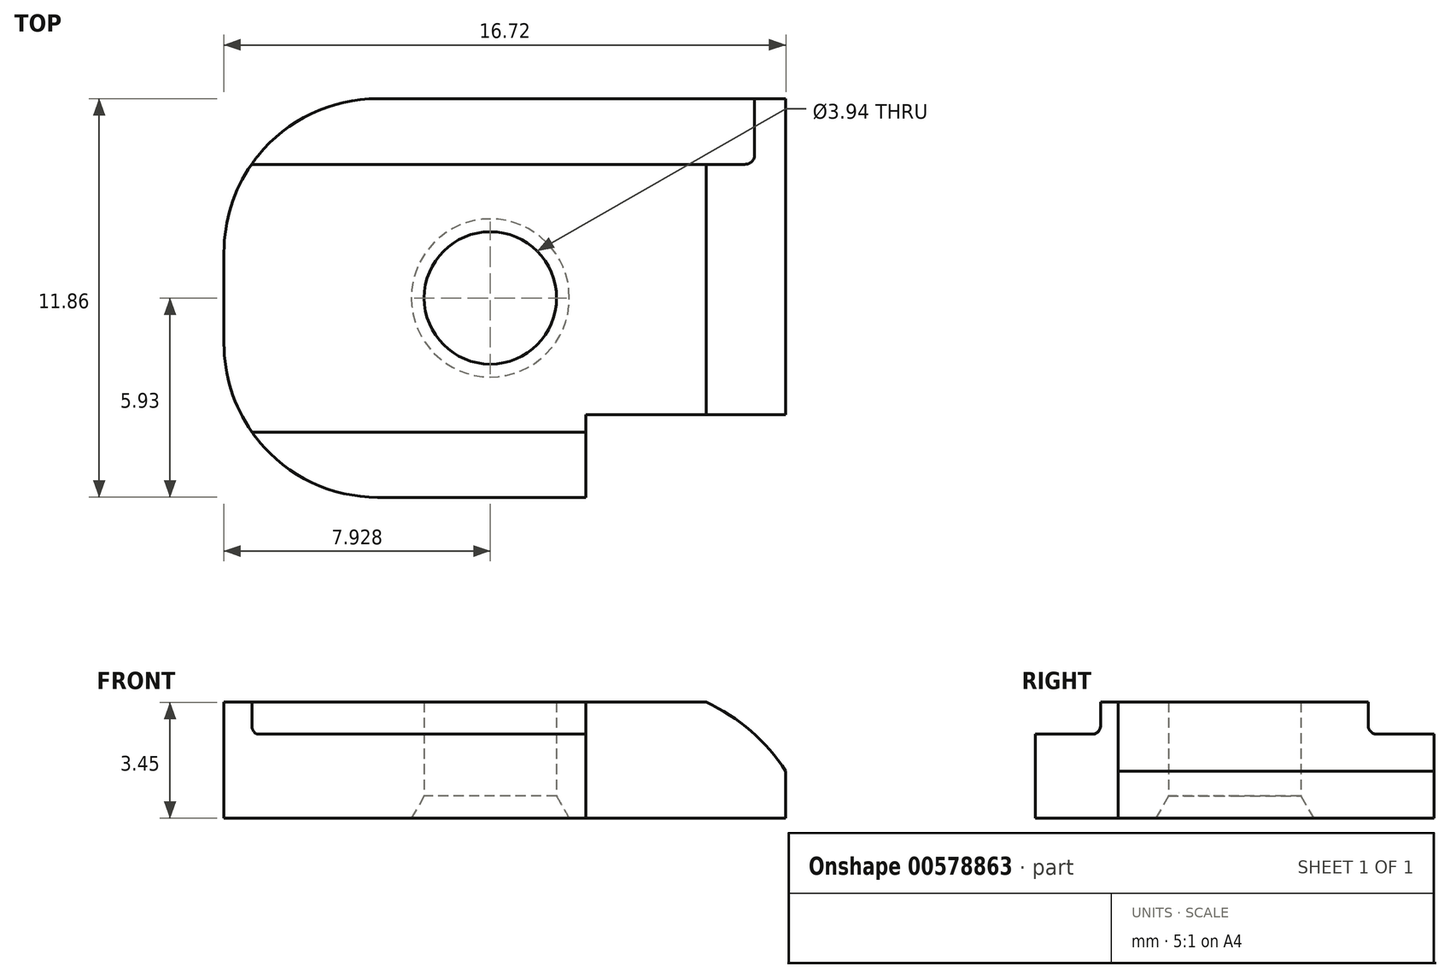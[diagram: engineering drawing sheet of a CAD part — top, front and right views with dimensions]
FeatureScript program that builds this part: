
annotation { "Feature Type Name" : "Feature", "Feature Type Description" : "" }
export const myFeature = defineFeature(function(context is Context, id is Id, definition is map)
    precondition{}
    {
        {
            var Q0;
            Q0=qCreatedBy(makeId("Top.planeOp"),FACE);
            var sketch = newSketch(context, id + "F0", { "sketchPlane" : qUnion([Q0])});
            skLineSegment(sketch, "E0.rect.bottom", {"start": v(-3.78, 5.93) * mm, "end": v(8.36, 5.93) * mm});
            skLineSegment(sketch, "E0.rect.top", {"start": v(-3.78, -5.93) * mm, "end": v(2.41, -5.93) * mm});
            skLineSegment(sketch, "E0.rect.left", {"start": v(-8.36, 1.36) * mm, "end": v(-8.36, -1.36) * mm});
            skLineSegment(sketch, "E0.rect.right", {"start": v(8.36, 5.93) * mm, "end": v(8.36, -3.47) * mm});
            skPoint(sketch, "E0.rect.middle", {"position": v(0, 0) * mm});
            skLineSegment(sketch, "E1", {"start": v(8.36, -3.47) * mm, "end": v(2.41, -3.47) * mm});
            skLineSegment(sketch, "E2", {"start": v(2.41, -3.47) * mm, "end": v(2.41, -5.93) * mm});
            skPoint(sketch, "E3.orphan", {"position": v(8.36, -5.93) * mm});
            skArc(sketch, "E4", {"start": v(-3.78, 5.93) * mm, "mid": v(-7.02, 4.6) * mm, "end": v(-8.36, 1.36) * mm});
            skPoint(sketch, "E5.orphan", {"position": v(-8.36, 5.93) * mm});
            skArc(sketch, "E6", {"start": v(-8.36, -1.36) * mm, "mid": v(-7.02, -4.6) * mm, "end": v(-3.78, -5.93) * mm});
            skPoint(sketch, "E7.orphan", {"position": v(-8.36, -5.93) * mm});
            skCircle(sketch, "E8", {"center": v(-0.43, 0) * mm, "radius": 1.97 * mm});
            skSolve(sketch);
        }
        {
            var Q0;
            Q0=makeQuery(id+"F0.imprint","IMPRINT",FACE,{"disambiguationData":[TD([[makeQuery(id+"F0.imprint","IMPRINT",EDGE,{"derivedFrom":sQuery(id+"F0.wireOp",EDGE,"E0.rect.bottom")}),-1.0]])]});
            extrude(context, id + "F1", {"entities" : qUnion([Q0]), "depth" : 3.45 * mm});
        }
        {
            var Q0;
            Q0=makeQuery(id+"F1.opExtrude","SWEPT_FACE",FACE,{"disambiguationData":[OSD([sQuery(id+"F0.wireOp",EDGE,"E0.rect.right")])]});
            var sketch = newSketch(context, id + "F2", { "sketchPlane" : qUnion([Q0])});
            skLineSegment(sketch, "E9.0", {"start": v(5.93, 3.45) * mm, "end": v(3.98, 3.45) * mm});
            skLineSegment(sketch, "E10.0", {"start": v(5.93, 3.45) * mm, "end": v(5.93, 2.5) * mm});
            skLineSegment(sketch, "E11", {"start": v(3.98, 3.45) * mm, "end": v(3.98, 2.5) * mm});
            skLineSegment(sketch, "E12", {"start": v(3.98, 2.5) * mm, "end": v(5.93, 2.5) * mm});
            skPoint(sketch, "E13.orphan", {"position": v(5.93, 0) * mm});
            skPoint(sketch, "E14", {"position": v(-3.99, 3.47) * mm});
            skLineSegment(sketch, "E15", {"start": v(-3.99, 3.47) * mm, "end": v(-3.99, 2.5) * mm});
            skLineSegment(sketch, "E16.0", {"start": v(-3.99, 3.45) * mm, "end": v(-5.93, 3.45) * mm});
            skLineSegment(sketch, "E17.0", {"start": v(-5.93, 3.45) * mm, "end": v(-5.93, 2.5) * mm});
            skLineSegment(sketch, "E18", {"start": v(-3.99, 2.5) * mm, "end": v(-5.93, 2.5) * mm});
            skSolve(sketch);
        }
        {
            var Q0;
            Q0=qSketchRegion(id+"F2",true);
            extrude(context, id + "F3", {"entities" : qUnion([Q0]), "operationType" : NewBodyOperationType.REMOVE, "endBound" : BoundingType.THROUGH_ALL, "oppositeDirection" : true, "depth" : 25.4 * mm});
        }
        {
            var Q0;
            Q0=qCreatedBy(makeId("Front.planeOp"),FACE);
            var sketch = newSketch(context, id + "F4", { "sketchPlane" : qUnion([Q0])});
            skLineSegment(sketch, "E19.0", {"start": v(8.36, 3.45) * mm, "end": v(5.99, 3.45) * mm});
            skLineSegment(sketch, "E20.0", {"start": v(8.36, 3.45) * mm, "end": v(8.36, 1.4) * mm});
            skArc(sketch, "E21", {"start": v(8.36, 1.4) * mm, "mid": v(7.32, 2.6) * mm, "end": v(5.99, 3.45) * mm});
            skPoint(sketch, "E22.orphan", {"position": v(2.41, 3.45) * mm});
            skPoint(sketch, "E23.orphan", {"position": v(8.36, 0) * mm});
            skSolve(sketch);
        }
        {
            var Q0;
            Q0=qSketchRegion(id+"F4",true);
            extrude(context, id + "F5", {"entities" : qUnion([Q0]), "operationType" : NewBodyOperationType.REMOVE, "endBound" : BoundingType.SYMMETRIC, "oppositeDirection" : true, "depth" : 25.4 * mm});
        }
        {
            var Q0;
            Q0=makeQuery(id+"F3.boolean.opBoolean","COPY",EDGE,{"derivedFrom":makeQuery(id+"F3.opExtrude","SWEPT_EDGE",EDGE,{"disambiguationData":[OSD([sQuery(id+"F2.wireOp",EDGE,"E15"),sQuery(id+"F2.wireOp",EDGE,"E16.0")])]})});
            var Q1;
            Q1=makeQuery(id+"F3.boolean.opBoolean","COPY",EDGE,{"derivedFrom":makeQuery(id+"F3.opExtrude","SWEPT_EDGE",EDGE,{"disambiguationData":[OSD([sQuery(id+"F0.wireOp",EDGE,"E0.rect.right"),sQuery(id+"F2.wireOp",EDGE,"E9.0"),sQuery(id+"F2.wireOp",EDGE,"E11")])]})});
            var Q2;
            Q2=makeQuery(id+"F3.boolean.opBoolean","COPY",EDGE,{"derivedFrom":makeQuery(id+"F3.opExtrude","SWEPT_EDGE",EDGE,{"disambiguationData":[OSD([sQuery(id+"F2.wireOp",EDGE,"E15"),sQuery(id+"F2.wireOp",EDGE,"E18")])]})});
            var Q3;
            Q3=makeQuery(id+"F3.boolean.opBoolean","COPY",EDGE,{"derivedFrom":makeQuery(id+"F3.opExtrude","SWEPT_EDGE",EDGE,{"disambiguationData":[OSD([sQuery(id+"F2.wireOp",EDGE,"E11"),sQuery(id+"F2.wireOp",EDGE,"E12")])]})});
            fillet(context, id + "F6", {"entities" : qUnion([Q0, Q1, Q2, Q3]), "radius" : 0.25 * mm, "tangentPropagation" : true, "allowEdgeOverflow" : false});
        }
        {
            var Q0;
            Q0=qCreatedBy(makeId("Front.planeOp"),FACE);
            var sketch = newSketch(context, id + "F7", { "sketchPlane" : qUnion([Q0])});
            skLineSegment(sketch, "E24.0", {"start": v(-2.78, 0) * mm, "end": v(-0.43, 0) * mm});
            skPoint(sketch, "E25", {"position": v(-0.43, 0) * mm});
            skLineSegment(sketch, "E26", {"start": v(-0.43, 0) * mm, "end": v(-0.43, 0.66) * mm});
            skLineSegment(sketch, "E27", {"start": v(-0.43, 0.66) * mm, "end": v(-2.4, 0.66) * mm});
            skLineSegment(sketch, "E28", {"start": v(-2.4, 0.66) * mm, "end": v(-2.78, 0) * mm});
            skPoint(sketch, "E29.0.end.orphan", {"position": v(-8.36, 0) * mm});
            skPoint(sketch, "E29.0.start.orphan", {"position": v(-8.36, 3.45) * mm});
            skPoint(sketch, "E30.orphan", {"position": v(-3.78, 0) * mm});
            skPoint(sketch, "E31.orphan", {"position": v(2.41, 0) * mm});
            skLineSegment(sketch, "E32.0", {"start": v(-8.36, 3.45) * mm, "end": v(-8.36, 0) * mm, "construction": true});
            skSolve(sketch);
        }
        {
            var Q0;
            Q0=qSketchRegion(id+"F7",true);
            var Q1;
            Q1=sQuery(id+"F7.wireOp",EDGE,"E26");
            revolve(context, id + "F8", {"operationType" : NewBodyOperationType.REMOVE, "entities" : qUnion([Q0]), "axis" : qUnion([Q1]), "revolveType" : RevolveType.FULL, "oppositeDirection" : true});
        }
    });
